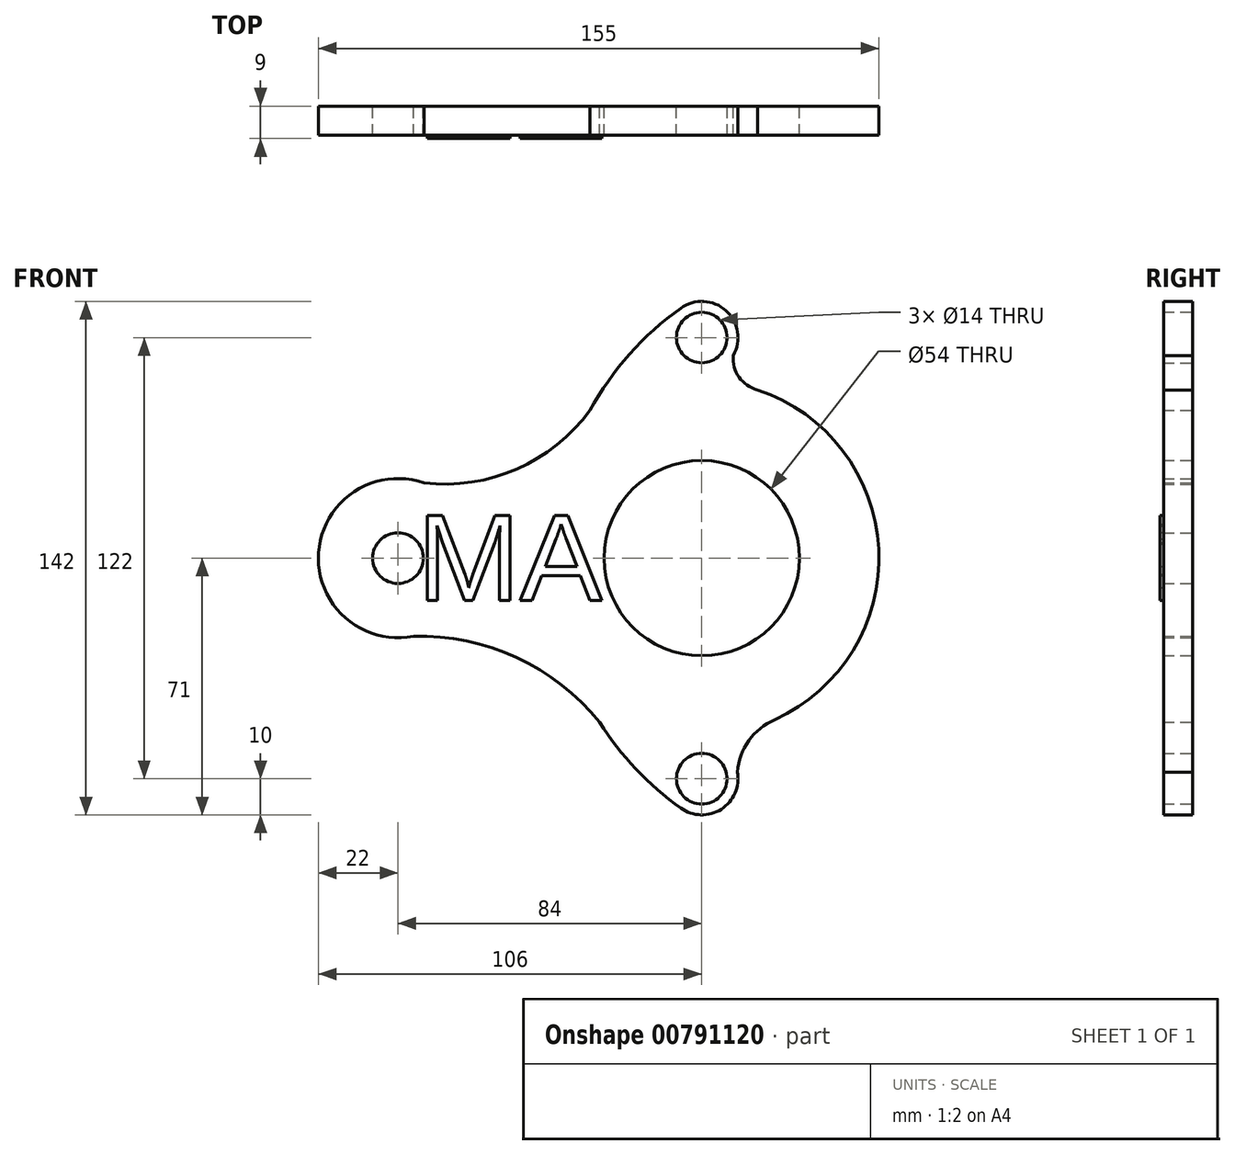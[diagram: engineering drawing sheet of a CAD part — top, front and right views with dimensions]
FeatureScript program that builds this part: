
annotation { "Feature Type Name" : "Feature", "Feature Type Description" : "" }
export const myFeature = defineFeature(function(context is Context, id is Id, definition is map)
    precondition{}
    {
        {
            var Q0;
            Q0=qCreatedBy(makeId("Front.planeOp"),FACE);
            var sketch = newSketch(context, id + "F0", { "sketchPlane" : qUnion([Q0])});
            skCircle(sketch, "E0", {"center": v(0, 0) * mm, "radius": 27 * mm});
            skArc(sketch, "E1", {"start": v(20.03, -44.72) * mm, "mid": v(48.9, 2.97) * mm, "end": v(14.47, 46.82) * mm});
            skLineSegment(sketch, "E2", {"start": v(0, 0) * mm, "end": v(-84, 0) * mm});
            skLineSegment(sketch, "E3", {"start": v(0, 0) * mm, "end": v(0, 61) * mm});
            skLineSegment(sketch, "E4", {"start": v(0, 0) * mm, "end": v(0, -61) * mm});
            skCircle(sketch, "E5", {"center": v(0, 61) * mm, "radius": 7 * mm});
            skCircle(sketch, "E6", {"center": v(0, 61) * mm, "radius": 10 * mm});
            skCircle(sketch, "E7", {"center": v(0, -61) * mm, "radius": 7 * mm});
            skCircle(sketch, "E8", {"center": v(0, -61) * mm, "radius": 10 * mm});
            skCircle(sketch, "E9", {"center": v(-84, 0) * mm, "radius": 7 * mm});
            skArc(sketch, "E10", {"start": v(-76.8, 20.79) * mm, "mid": v(-105.95, 1.52) * mm, "end": v(-79.74, -21.58) * mm});
            skArc(sketch, "E11", {"start": v(-5.82, 69.13) * mm, "mid": v(-19.96, 56.4) * mm, "end": v(-30.92, 40.83) * mm});
            skArc(sketch, "E12", {"start": v(-76.8, 20.79) * mm, "mid": v(-51.16, 24.63) * mm, "end": v(-30.92, 40.83) * mm});
            skArc(sketch, "E13", {"start": v(-28.24, -45.37) * mm, "mid": v(-51.22, -27.47) * mm, "end": v(-79.74, -21.58) * mm});
            skArc(sketch, "E14", {"start": v(8.68, 56.04) * mm, "mid": v(10.3, 50.05) * mm, "end": v(15.41, 46.51) * mm});
            skArc(sketch, "E15", {"start": v(20.14, -44.67) * mm, "mid": v(13, -50.5) * mm, "end": v(9.83, -59.14) * mm});
            skArc(sketch, "E16.trimOffspring", {"start": v(-28.24, -45.37) * mm, "mid": v(-18.18, -58.34) * mm, "end": v(-5.82, -69.13) * mm});
            skSolve(sketch);
        }
        {
            var Q0;
            Q0=makeQuery(id+"F0.imprint","IMPRINT",FACE,{"disambiguationData":[TD([[makeQuery(id+"F0.imprint","IMPRINT",EDGE,{"derivedFrom":sQuery(id+"F0.wireOp",EDGE,"E9")}),-1.0]])]});
            var Q1;
            {var subQ3=sQuery(id+"F0.wireOp",EDGE,"E0");var subQ12=sQuery(id+"F0.wireOp",EDGE,"E3");var subQ14=makeQuery(id+"F0.imprint","INTERSECT",VERTEX,{"derivedFrom":[subQ3,subQ12]});Q1=makeQuery(id+"F0.imprint","IMPRINT",FACE,{"disambiguationData":[TD([[makeQuery(id+"F0.imprint","IMPRINT",EDGE,{"disambiguationData":[TD([[subQ14,1.0]])],"derivedFrom":subQ3}),-1.0]])]});}
            var Q2;
            Q2=makeQuery(id+"F0.imprint","IMPRINT",FACE,{"disambiguationData":[TD([[makeQuery(id+"F0.imprint","IMPRINT",EDGE,{"derivedFrom":sQuery(id+"F0.wireOp",EDGE,"E7")}),-1.0]])]});
            var Q3;
            Q3=makeQuery(id+"F0.imprint","IMPRINT",FACE,{"disambiguationData":[TD([[makeQuery(id+"F0.imprint","IMPRINT",EDGE,{"derivedFrom":sQuery(id+"F0.wireOp",EDGE,"E5")}),-1.0]])]});
            extrude(context, id + "F1", {"entities" : qUnion([Q0, Q1, Q2, Q3]), "depth" : 8 * mm, "offsetDistance" : 25 * mm});
        }
        {
            var Q0;
            Q0=makeQuery(id+"F1.opExtrude","CAP_FACE",FACE,{"disambiguationData":[OSD([sQuery(id+"F0.wireOp",EDGE,"E0"),sQuery(id+"F0.wireOp",EDGE,"E1"),sQuery(id+"F0.wireOp",EDGE,"E5"),sQuery(id+"F0.wireOp",EDGE,"E6"),sQuery(id+"F0.wireOp",EDGE,"E7"),sQuery(id+"F0.wireOp",EDGE,"E8"),sQuery(id+"F0.wireOp",EDGE,"E9"),sQuery(id+"F0.wireOp",EDGE,"E10"),sQuery(id+"F0.wireOp",EDGE,"E11"),sQuery(id+"F0.wireOp",EDGE,"E12"),sQuery(id+"F0.wireOp",EDGE,"E13"),sQuery(id+"F0.wireOp",EDGE,"E14"),sQuery(id+"F0.wireOp",EDGE,"E15"),sQuery(id+"F0.wireOp",EDGE,"E16.trimOffspring")])],"isStart":false});
            var sketch = newSketch(context, id + "F2", { "sketchPlane" : qUnion([Q0])});
            skText(sketch, "E17", { "text": "MA", "fontName": "Arimo-Regular.ttf"});
            const initialGuessF2  = {"E17": [-0.07866, -0.01166, 1, 0, 0.02453]};
            skSetInitialGuess(sketch, initialGuessF2);
            skSolve(sketch);
        }
        {
            var Q0;
            Q0 = qSketchRegion(id + "F2", true);
            extrude(context, id + "F3", {"entities" : qUnion([Q0]), "operationType" : NewBodyOperationType.ADD, "depth" : 1 * mm, "offsetDistance" : 25 * mm});
        }
    });
